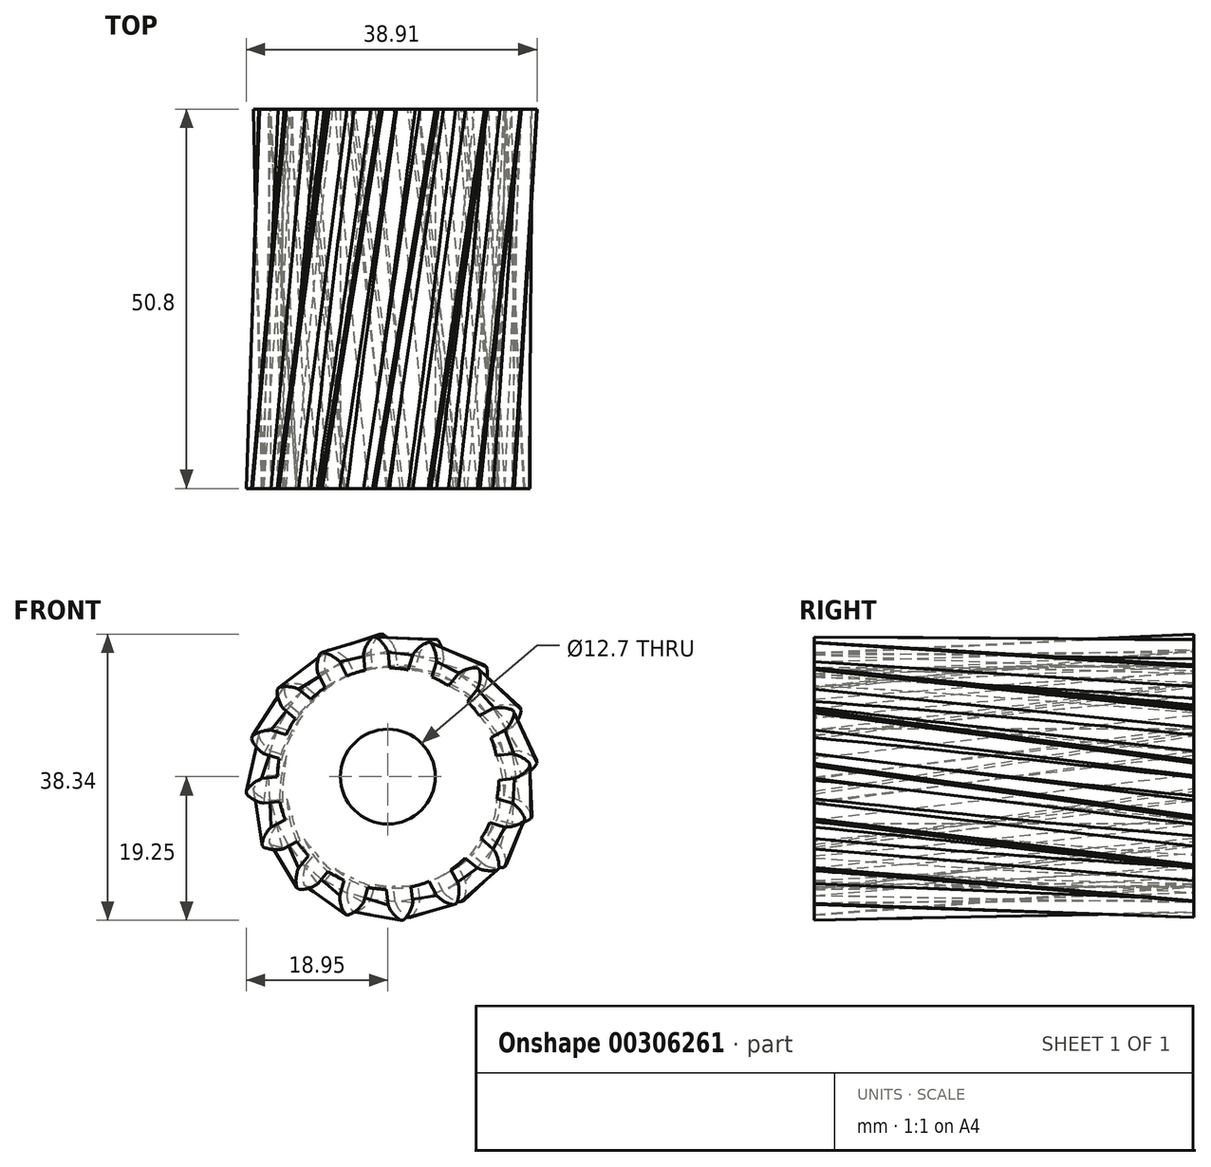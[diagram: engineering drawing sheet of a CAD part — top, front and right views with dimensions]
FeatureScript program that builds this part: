
annotation { "Feature Type Name" : "Feature", "Feature Type Description" : "" }
export const myFeature = defineFeature(function(context is Context, id is Id, definition is map)
    precondition{}
    {
        {
            var Q0;
            Q0=qCreatedBy(makeId("Front.planeOp"),FACE);
            var sketch = newSketch(context, id + "F0", { "sketchPlane" : qUnion([Q0])});
            skCircle(sketch, "E0", {"center": v(0.98, 0.11) * mm, "radius": 14.82 * mm});
            skArc(sketch, "E1.trimOffspring", {"start": v(0.98, 17.04) * mm, "mid": v(0.3, 18.2) * mm, "end": v(-0.7, 19.09) * mm});
            skLineSegment(sketch, "E2", {"start": v(0.98, 17.04) * mm, "end": v(1.19, 14.93) * mm});
            skLineSegment(sketch, "E3", {"start": v(-0.7, 19.09) * mm, "end": v(-0.89, 19.07) * mm});
            skLineSegment(sketch, "E4.MirrorCS", {"start": v(-1.08, 19.05) * mm, "end": v(-0.89, 19.07) * mm});
            skArc(sketch, "E5.MirrorCS", {"start": v(-2.32, 16.71) * mm, "mid": v(-1.89, 17.98) * mm, "end": v(-1.08, 19.05) * mm});
            skLineSegment(sketch, "E6.MirrorCS", {"start": v(-2.32, 16.71) * mm, "end": v(-2.12, 14.6) * mm});
            skPoint(sketch, "E7.orphan", {"position": v(-2, 13.45) * mm});
            skPoint(sketch, "E8.orphan", {"position": v(1.3, 13.77) * mm});
            skLineSegment(sketch, "E9.1.0", {"start": v(-8.43, 14.19) * mm, "end": v(-7.43, 12.32) * mm});
            skArc(sketch, "E9.1.1", {"start": v(-8.43, 14.19) * mm, "mid": v(-8.51, 15.52) * mm, "end": v(-8.17, 16.82) * mm});
            skLineSegment(sketch, "E9.1.2", {"start": v(-7.83, 17) * mm, "end": v(-8, 16.91) * mm});
            skLineSegment(sketch, "E9.1.3", {"start": v(-8.17, 16.82) * mm, "end": v(-8, 16.91) * mm});
            skArc(sketch, "E9.1.4", {"start": v(-5.5, 15.75) * mm, "mid": v(-6.56, 16.56) * mm, "end": v(-7.83, 17) * mm});
            skLineSegment(sketch, "E9.1.5", {"start": v(-5.5, 15.75) * mm, "end": v(-4.5, 13.88) * mm});
            skLineSegment(sketch, "E9.2.0", {"start": v(-13.1, 9.52) * mm, "end": v(-11.46, 8.17) * mm});
            skArc(sketch, "E9.2.1", {"start": v(-13.1, 9.52) * mm, "mid": v(-13.69, 10.72) * mm, "end": v(-13.87, 12.04) * mm});
            skLineSegment(sketch, "E9.2.2", {"start": v(-13.62, 12.35) * mm, "end": v(-13.75, 12.2) * mm});
            skLineSegment(sketch, "E9.2.3", {"start": v(-13.87, 12.04) * mm, "end": v(-13.75, 12.2) * mm});
            skArc(sketch, "E9.2.4", {"start": v(-11, 12.08) * mm, "mid": v(-12.29, 12.42) * mm, "end": v(-13.62, 12.35) * mm});
            skLineSegment(sketch, "E9.2.5", {"start": v(-11, 12.08) * mm, "end": v(-9.35, 10.74) * mm});
            skLineSegment(sketch, "E9.3.0", {"start": v(-15.62, 3.41) * mm, "end": v(-13.6, 2.8) * mm});
            skArc(sketch, "E9.3.1", {"start": v(-15.62, 3.41) * mm, "mid": v(-16.63, 4.3) * mm, "end": v(-17.3, 5.45) * mm});
            skLineSegment(sketch, "E9.3.2", {"start": v(-17.2, 5.83) * mm, "end": v(-17.25, 5.64) * mm});
            skLineSegment(sketch, "E9.3.3", {"start": v(-17.3, 5.45) * mm, "end": v(-17.25, 5.64) * mm});
            skArc(sketch, "E9.3.4", {"start": v(-14.66, 6.59) * mm, "mid": v(-15.99, 6.41) * mm, "end": v(-17.2, 5.83) * mm});
            skLineSegment(sketch, "E9.3.5", {"start": v(-14.66, 6.59) * mm, "end": v(-12.63, 5.97) * mm});
            skLineSegment(sketch, "E9.4.0", {"start": v(-15.62, -3.2) * mm, "end": v(-13.52, -2.98) * mm});
            skArc(sketch, "E9.4.1", {"start": v(-15.62, -3.2) * mm, "mid": v(-16.9, -2.76) * mm, "end": v(-17.96, -1.95) * mm});
            skLineSegment(sketch, "E9.4.2", {"start": v(-18, -1.56) * mm, "end": v(-17.98, -1.76) * mm});
            skLineSegment(sketch, "E9.4.3", {"start": v(-17.96, -1.95) * mm, "end": v(-17.98, -1.76) * mm});
            skArc(sketch, "E9.4.4", {"start": v(-15.95, 0.11) * mm, "mid": v(-17.1, -0.56) * mm, "end": v(-18, -1.56) * mm});
            skLineSegment(sketch, "E9.4.5", {"start": v(-15.95, 0.11) * mm, "end": v(-13.84, 0.32) * mm});
            skLineSegment(sketch, "E9.5.0", {"start": v(-13.1, -9.3) * mm, "end": v(-11.23, -8.3) * mm});
            skArc(sketch, "E9.5.1", {"start": v(-13.1, -9.3) * mm, "mid": v(-14.43, -9.38) * mm, "end": v(-15.73, -9.04) * mm});
            skLineSegment(sketch, "E9.5.2", {"start": v(-15.91, -8.7) * mm, "end": v(-15.82, -8.87) * mm});
            skLineSegment(sketch, "E9.5.3", {"start": v(-15.73, -9.04) * mm, "end": v(-15.82, -8.87) * mm});
            skArc(sketch, "E9.5.4", {"start": v(-14.66, -6.37) * mm, "mid": v(-15.47, -7.43) * mm, "end": v(-15.91, -8.7) * mm});
            skLineSegment(sketch, "E9.5.5", {"start": v(-14.66, -6.37) * mm, "end": v(-12.8, -5.37) * mm});
            skLineSegment(sketch, "E9.6.0", {"start": v(-8.43, -13.97) * mm, "end": v(-7.08, -12.33) * mm});
            skArc(sketch, "E9.6.1", {"start": v(-8.43, -13.97) * mm, "mid": v(-9.63, -14.55) * mm, "end": v(-10.95, -14.74) * mm});
            skLineSegment(sketch, "E9.6.2", {"start": v(-11.26, -14.5) * mm, "end": v(-11.1, -14.62) * mm});
            skLineSegment(sketch, "E9.6.3", {"start": v(-10.95, -14.74) * mm, "end": v(-11.1, -14.62) * mm});
            skArc(sketch, "E9.6.4", {"start": v(-11, -11.86) * mm, "mid": v(-11.33, -13.15) * mm, "end": v(-11.26, -14.5) * mm});
            skLineSegment(sketch, "E9.6.5", {"start": v(-11, -11.86) * mm, "end": v(-9.65, -10.22) * mm});
            skLineSegment(sketch, "E9.7.0", {"start": v(-2.32, -16.5) * mm, "end": v(-1.7, -14.46) * mm});
            skArc(sketch, "E9.7.1", {"start": v(-2.32, -16.5) * mm, "mid": v(-3.2, -17.5) * mm, "end": v(-4.36, -18.17) * mm});
            skLineSegment(sketch, "E9.7.2", {"start": v(-4.74, -18.06) * mm, "end": v(-4.55, -18.12) * mm});
            skLineSegment(sketch, "E9.7.3", {"start": v(-4.36, -18.17) * mm, "end": v(-4.55, -18.12) * mm});
            skArc(sketch, "E9.7.4", {"start": v(-5.5, -15.53) * mm, "mid": v(-5.32, -16.86) * mm, "end": v(-4.74, -18.06) * mm});
            skLineSegment(sketch, "E9.7.5", {"start": v(-5.5, -15.53) * mm, "end": v(-4.88, -13.5) * mm});
            skLineSegment(sketch, "E9.8.0", {"start": v(4.28, -16.5) * mm, "end": v(4.07, -14.38) * mm});
            skArc(sketch, "E9.8.1", {"start": v(4.28, -16.5) * mm, "mid": v(3.85, -17.76) * mm, "end": v(3.04, -18.83) * mm});
            skLineSegment(sketch, "E9.8.2", {"start": v(2.65, -18.87) * mm, "end": v(2.85, -18.85) * mm});
            skLineSegment(sketch, "E9.8.3", {"start": v(3.04, -18.83) * mm, "end": v(2.85, -18.85) * mm});
            skArc(sketch, "E9.8.4", {"start": v(0.98, -16.82) * mm, "mid": v(1.65, -17.98) * mm, "end": v(2.65, -18.87) * mm});
            skLineSegment(sketch, "E9.8.5", {"start": v(0.98, -16.82) * mm, "end": v(0.77, -14.7) * mm});
            skLineSegment(sketch, "E9.9.0", {"start": v(10.38, -13.97) * mm, "end": v(9.39, -12.1) * mm});
            skArc(sketch, "E9.9.1", {"start": v(10.38, -13.97) * mm, "mid": v(10.47, -15.3) * mm, "end": v(10.13, -16.6) * mm});
            skLineSegment(sketch, "E9.9.2", {"start": v(9.79, -16.78) * mm, "end": v(9.96, -16.7) * mm});
            skLineSegment(sketch, "E9.9.3", {"start": v(10.13, -16.6) * mm, "end": v(9.96, -16.7) * mm});
            skArc(sketch, "E9.9.4", {"start": v(7.46, -15.53) * mm, "mid": v(8.52, -16.34) * mm, "end": v(9.79, -16.78) * mm});
            skLineSegment(sketch, "E9.9.5", {"start": v(7.46, -15.53) * mm, "end": v(6.46, -13.66) * mm});
            skLineSegment(sketch, "E9.10.0", {"start": v(15.06, -9.3) * mm, "end": v(13.42, -7.95) * mm});
            skArc(sketch, "E9.10.1", {"start": v(15.06, -9.3) * mm, "mid": v(15.64, -10.5) * mm, "end": v(15.83, -11.82) * mm});
            skLineSegment(sketch, "E9.10.2", {"start": v(15.58, -12.12) * mm, "end": v(15.7, -11.97) * mm});
            skLineSegment(sketch, "E9.10.3", {"start": v(15.83, -11.82) * mm, "end": v(15.7, -11.97) * mm});
            skArc(sketch, "E9.10.4", {"start": v(12.95, -11.86) * mm, "mid": v(14.24, -12.2) * mm, "end": v(15.58, -12.12) * mm});
            skLineSegment(sketch, "E9.10.5", {"start": v(12.95, -11.86) * mm, "end": v(11.31, -10.51) * mm});
            skLineSegment(sketch, "E9.11.0", {"start": v(17.58, -3.2) * mm, "end": v(15.55, -2.58) * mm});
            skArc(sketch, "E9.11.1", {"start": v(17.58, -3.2) * mm, "mid": v(18.59, -4.08) * mm, "end": v(19.26, -5.23) * mm});
            skLineSegment(sketch, "E9.11.2", {"start": v(19.15, -5.6) * mm, "end": v(19.2, -5.42) * mm});
            skLineSegment(sketch, "E9.11.3", {"start": v(19.26, -5.23) * mm, "end": v(19.2, -5.42) * mm});
            skArc(sketch, "E9.11.4", {"start": v(16.62, -6.37) * mm, "mid": v(17.95, -6.19) * mm, "end": v(19.15, -5.6) * mm});
            skLineSegment(sketch, "E9.11.5", {"start": v(16.62, -6.37) * mm, "end": v(14.6, -5.75) * mm});
            skLineSegment(sketch, "E9.12.0", {"start": v(17.58, 3.41) * mm, "end": v(15.47, 3.2) * mm});
            skArc(sketch, "E9.12.1", {"start": v(17.58, 3.41) * mm, "mid": v(18.85, 2.98) * mm, "end": v(19.92, 2.17) * mm});
            skLineSegment(sketch, "E9.12.2", {"start": v(19.96, 1.78) * mm, "end": v(19.94, 1.98) * mm});
            skLineSegment(sketch, "E9.12.3", {"start": v(19.92, 2.17) * mm, "end": v(19.94, 1.98) * mm});
            skArc(sketch, "E9.12.4", {"start": v(17.9, 0.11) * mm, "mid": v(19.07, 0.78) * mm, "end": v(19.96, 1.78) * mm});
            skLineSegment(sketch, "E9.12.5", {"start": v(17.9, 0.11) * mm, "end": v(15.8, -0.1) * mm});
            skLineSegment(sketch, "E9.13.0", {"start": v(15.06, 9.52) * mm, "end": v(13.19, 8.52) * mm});
            skArc(sketch, "E9.13.1", {"start": v(15.06, 9.52) * mm, "mid": v(16.4, 9.6) * mm, "end": v(17.69, 9.26) * mm});
            skLineSegment(sketch, "E9.13.2", {"start": v(17.87, 8.92) * mm, "end": v(17.78, 9.1) * mm});
            skLineSegment(sketch, "E9.13.3", {"start": v(17.69, 9.26) * mm, "end": v(17.78, 9.1) * mm});
            skArc(sketch, "E9.13.4", {"start": v(16.62, 6.59) * mm, "mid": v(17.43, 7.65) * mm, "end": v(17.87, 8.92) * mm});
            skLineSegment(sketch, "E9.13.5", {"start": v(16.62, 6.59) * mm, "end": v(14.75, 5.6) * mm});
            skLineSegment(sketch, "E9.14.0", {"start": v(10.38, 14.19) * mm, "end": v(9.04, 12.55) * mm});
            skArc(sketch, "E9.14.1", {"start": v(10.38, 14.19) * mm, "mid": v(11.59, 14.78) * mm, "end": v(12.91, 14.96) * mm});
            skLineSegment(sketch, "E9.14.2", {"start": v(13.21, 14.71) * mm, "end": v(13.06, 14.84) * mm});
            skLineSegment(sketch, "E9.14.3", {"start": v(12.91, 14.96) * mm, "end": v(13.06, 14.84) * mm});
            skArc(sketch, "E9.14.4", {"start": v(12.95, 12.08) * mm, "mid": v(13.3, 13.38) * mm, "end": v(13.21, 14.71) * mm});
            skLineSegment(sketch, "E9.14.5", {"start": v(12.95, 12.08) * mm, "end": v(11.6, 10.44) * mm});
            skLineSegment(sketch, "E9.15.0", {"start": v(4.28, 16.71) * mm, "end": v(3.67, 14.69) * mm});
            skArc(sketch, "E9.15.1", {"start": v(4.28, 16.71) * mm, "mid": v(5.17, 17.72) * mm, "end": v(6.32, 18.4) * mm});
            skLineSegment(sketch, "E9.15.2", {"start": v(6.7, 18.28) * mm, "end": v(6.5, 18.34) * mm});
            skLineSegment(sketch, "E9.15.3", {"start": v(6.32, 18.4) * mm, "end": v(6.5, 18.34) * mm});
            skArc(sketch, "E9.15.4", {"start": v(7.46, 15.75) * mm, "mid": v(7.28, 17.08) * mm, "end": v(6.7, 18.28) * mm});
            skLineSegment(sketch, "E9.15.5", {"start": v(7.46, 15.75) * mm, "end": v(6.84, 13.72) * mm});
            skSolve(sketch);
        }
        {
            var Q0;
            Q0=qCreatedBy(makeId("Front.planeOp"),FACE);
            cPlane(context, id + "F1", {"entities" : qUnion([Q0]), "cplaneType" : CPlaneType.OFFSET, "offset" : 50.8 * mm, "width" : 152.4 * mm, "height" : 152.4 * mm});
        }
        {
            var Q0;
            Q0=qCreatedBy(id+"F1.planeOp",FACE);
            var sketch = newSketch(context, id + "F2", { "sketchPlane" : qUnion([Q0])});
            skCircle(sketch, "E10", {"center": v(0.03, -0.27) * mm, "radius": 14.82 * mm});
            skArc(sketch, "E11.trimOffspring", {"start": v(0.03, 16.66) * mm, "mid": v(-0.65, 17.82) * mm, "end": v(-1.65, 18.7) * mm});
            skLineSegment(sketch, "E12", {"start": v(0.03, 16.66) * mm, "end": v(0.23, 14.55) * mm});
            skLineSegment(sketch, "E13", {"start": v(-1.65, 18.7) * mm, "end": v(-1.84, 18.69) * mm});
            skLineSegment(sketch, "E14.MirrorCS", {"start": v(-2.03, 18.67) * mm, "end": v(-1.84, 18.69) * mm});
            skArc(sketch, "E15.MirrorCS", {"start": v(-3.28, 16.33) * mm, "mid": v(-2.84, 17.6) * mm, "end": v(-2.03, 18.67) * mm});
            skLineSegment(sketch, "E16.MirrorCS", {"start": v(-3.28, 16.33) * mm, "end": v(-3.07, 14.22) * mm});
            skPoint(sketch, "E17.orphan", {"position": v(-2.95, 13.07) * mm});
            skPoint(sketch, "E18.orphan", {"position": v(0.35, 13.4) * mm});
            skLineSegment(sketch, "E19.1.0", {"start": v(-9.38, 13.8) * mm, "end": v(-8.38, 11.94) * mm});
            skArc(sketch, "E19.1.1", {"start": v(-9.38, 13.8) * mm, "mid": v(-9.46, 15.14) * mm, "end": v(-9.12, 16.44) * mm});
            skLineSegment(sketch, "E19.1.2", {"start": v(-8.78, 16.62) * mm, "end": v(-8.95, 16.53) * mm});
            skLineSegment(sketch, "E19.1.3", {"start": v(-9.12, 16.44) * mm, "end": v(-8.95, 16.53) * mm});
            skArc(sketch, "E19.1.4", {"start": v(-6.45, 15.37) * mm, "mid": v(-7.52, 16.18) * mm, "end": v(-8.78, 16.62) * mm});
            skLineSegment(sketch, "E19.1.5", {"start": v(-6.45, 15.37) * mm, "end": v(-5.45, 13.5) * mm});
            skLineSegment(sketch, "E19.2.0", {"start": v(-14.05, 9.14) * mm, "end": v(-12.41, 7.8) * mm});
            skArc(sketch, "E19.2.1", {"start": v(-14.05, 9.14) * mm, "mid": v(-14.64, 10.34) * mm, "end": v(-14.82, 11.66) * mm});
            skLineSegment(sketch, "E19.2.2", {"start": v(-14.57, 11.97) * mm, "end": v(-14.7, 11.82) * mm});
            skLineSegment(sketch, "E19.2.3", {"start": v(-14.82, 11.66) * mm, "end": v(-14.7, 11.82) * mm});
            skArc(sketch, "E19.2.4", {"start": v(-11.94, 11.7) * mm, "mid": v(-13.24, 12.04) * mm, "end": v(-14.57, 11.97) * mm});
            skLineSegment(sketch, "E19.2.5", {"start": v(-11.94, 11.7) * mm, "end": v(-10.3, 10.36) * mm});
            skLineSegment(sketch, "E19.3.0", {"start": v(-16.58, 3.03) * mm, "end": v(-14.55, 2.42) * mm});
            skArc(sketch, "E19.3.1", {"start": v(-16.58, 3.03) * mm, "mid": v(-17.58, 3.92) * mm, "end": v(-18.26, 5.07) * mm});
            skLineSegment(sketch, "E19.3.2", {"start": v(-18.15, 5.45) * mm, "end": v(-18.2, 5.26) * mm});
            skLineSegment(sketch, "E19.3.3", {"start": v(-18.26, 5.07) * mm, "end": v(-18.2, 5.26) * mm});
            skArc(sketch, "E19.3.4", {"start": v(-15.61, 6.2) * mm, "mid": v(-16.94, 6.03) * mm, "end": v(-18.15, 5.45) * mm});
            skLineSegment(sketch, "E19.3.5", {"start": v(-15.61, 6.2) * mm, "end": v(-13.59, 5.6) * mm});
            skLineSegment(sketch, "E19.4.0", {"start": v(-16.58, -3.57) * mm, "end": v(-14.47, -3.36) * mm});
            skArc(sketch, "E19.4.1", {"start": v(-16.58, -3.57) * mm, "mid": v(-17.84, -3.14) * mm, "end": v(-18.91, -2.33) * mm});
            skLineSegment(sketch, "E19.4.2", {"start": v(-18.95, -1.94) * mm, "end": v(-18.93, -2.14) * mm});
            skLineSegment(sketch, "E19.4.3", {"start": v(-18.91, -2.33) * mm, "end": v(-18.93, -2.14) * mm});
            skArc(sketch, "E19.4.4", {"start": v(-16.9, -0.27) * mm, "mid": v(-18.06, -0.94) * mm, "end": v(-18.95, -1.94) * mm});
            skLineSegment(sketch, "E19.4.5", {"start": v(-16.9, -0.27) * mm, "end": v(-14.8, -0.06) * mm});
            skLineSegment(sketch, "E19.5.0", {"start": v(-14.05, -9.68) * mm, "end": v(-12.18, -8.68) * mm});
            skArc(sketch, "E19.5.1", {"start": v(-14.05, -9.68) * mm, "mid": v(-15.39, -9.76) * mm, "end": v(-16.68, -9.42) * mm});
            skLineSegment(sketch, "E19.5.2", {"start": v(-16.87, -9.08) * mm, "end": v(-16.77, -9.25) * mm});
            skLineSegment(sketch, "E19.5.3", {"start": v(-16.68, -9.42) * mm, "end": v(-16.77, -9.25) * mm});
            skArc(sketch, "E19.5.4", {"start": v(-15.61, -6.75) * mm, "mid": v(-16.43, -7.81) * mm, "end": v(-16.87, -9.08) * mm});
            skLineSegment(sketch, "E19.5.5", {"start": v(-15.61, -6.75) * mm, "end": v(-13.74, -5.75) * mm});
            skLineSegment(sketch, "E19.6.0", {"start": v(-9.38, -14.35) * mm, "end": v(-8.03, -12.7) * mm});
            skArc(sketch, "E19.6.1", {"start": v(-9.38, -14.35) * mm, "mid": v(-10.58, -14.94) * mm, "end": v(-11.9, -15.12) * mm});
            skLineSegment(sketch, "E19.6.2", {"start": v(-12.2, -14.87) * mm, "end": v(-12.06, -15) * mm});
            skLineSegment(sketch, "E19.6.3", {"start": v(-11.9, -15.12) * mm, "end": v(-12.06, -15) * mm});
            skArc(sketch, "E19.6.4", {"start": v(-11.94, -12.24) * mm, "mid": v(-12.29, -13.53) * mm, "end": v(-12.2, -14.87) * mm});
            skLineSegment(sketch, "E19.6.5", {"start": v(-11.94, -12.24) * mm, "end": v(-10.6, -10.6) * mm});
            skLineSegment(sketch, "E19.7.0", {"start": v(-3.28, -16.87) * mm, "end": v(-2.66, -14.85) * mm});
            skArc(sketch, "E19.7.1", {"start": v(-3.28, -16.87) * mm, "mid": v(-4.16, -17.88) * mm, "end": v(-5.32, -18.56) * mm});
            skLineSegment(sketch, "E19.7.2", {"start": v(-5.69, -18.44) * mm, "end": v(-5.5, -18.5) * mm});
            skLineSegment(sketch, "E19.7.3", {"start": v(-5.32, -18.56) * mm, "end": v(-5.5, -18.5) * mm});
            skArc(sketch, "E19.7.4", {"start": v(-6.45, -15.91) * mm, "mid": v(-6.27, -17.24) * mm, "end": v(-5.69, -18.44) * mm});
            skLineSegment(sketch, "E19.7.5", {"start": v(-6.45, -15.91) * mm, "end": v(-5.84, -13.88) * mm});
            skLineSegment(sketch, "E19.8.0", {"start": v(3.33, -16.87) * mm, "end": v(3.12, -14.76) * mm});
            skArc(sketch, "E19.8.1", {"start": v(3.33, -16.87) * mm, "mid": v(2.9, -18.14) * mm, "end": v(2.09, -19.2) * mm});
            skLineSegment(sketch, "E19.8.2", {"start": v(1.7, -19.25) * mm, "end": v(1.9, -19.23) * mm});
            skLineSegment(sketch, "E19.8.3", {"start": v(2.09, -19.2) * mm, "end": v(1.9, -19.23) * mm});
            skArc(sketch, "E19.8.4", {"start": v(0.03, -17.2) * mm, "mid": v(0.7, -18.36) * mm, "end": v(1.7, -19.25) * mm});
            skLineSegment(sketch, "E19.8.5", {"start": v(0.03, -17.2) * mm, "end": v(-0.18, -15.09) * mm});
            skLineSegment(sketch, "E19.9.0", {"start": v(9.43, -14.35) * mm, "end": v(8.43, -12.48) * mm});
            skArc(sketch, "E19.9.1", {"start": v(9.43, -14.35) * mm, "mid": v(9.52, -15.68) * mm, "end": v(9.18, -16.98) * mm});
            skLineSegment(sketch, "E19.9.2", {"start": v(8.83, -17.16) * mm, "end": v(9, -17.07) * mm});
            skLineSegment(sketch, "E19.9.3", {"start": v(9.18, -16.98) * mm, "end": v(9, -17.07) * mm});
            skArc(sketch, "E19.9.4", {"start": v(6.5, -15.91) * mm, "mid": v(7.57, -16.72) * mm, "end": v(8.83, -17.16) * mm});
            skLineSegment(sketch, "E19.9.5", {"start": v(6.5, -15.91) * mm, "end": v(5.5, -14.04) * mm});
            skLineSegment(sketch, "E19.10.0", {"start": v(14.1, -9.68) * mm, "end": v(12.46, -8.33) * mm});
            skArc(sketch, "E19.10.1", {"start": v(14.1, -9.68) * mm, "mid": v(14.7, -10.88) * mm, "end": v(14.88, -12.2) * mm});
            skLineSegment(sketch, "E19.10.2", {"start": v(14.63, -12.5) * mm, "end": v(14.75, -12.36) * mm});
            skLineSegment(sketch, "E19.10.3", {"start": v(14.88, -12.2) * mm, "end": v(14.75, -12.36) * mm});
            skArc(sketch, "E19.10.4", {"start": v(12, -12.24) * mm, "mid": v(13.3, -12.58) * mm, "end": v(14.63, -12.5) * mm});
            skLineSegment(sketch, "E19.10.5", {"start": v(12, -12.24) * mm, "end": v(10.36, -10.9) * mm});
            skLineSegment(sketch, "E19.11.0", {"start": v(16.63, -3.57) * mm, "end": v(14.6, -2.96) * mm});
            skArc(sketch, "E19.11.1", {"start": v(16.63, -3.57) * mm, "mid": v(17.63, -4.46) * mm, "end": v(18.31, -5.61) * mm});
            skLineSegment(sketch, "E19.11.2", {"start": v(18.2, -5.99) * mm, "end": v(18.26, -5.8) * mm});
            skLineSegment(sketch, "E19.11.3", {"start": v(18.31, -5.61) * mm, "end": v(18.26, -5.8) * mm});
            skArc(sketch, "E19.11.4", {"start": v(15.67, -6.75) * mm, "mid": v(17, -6.57) * mm, "end": v(18.2, -5.99) * mm});
            skLineSegment(sketch, "E19.11.5", {"start": v(15.67, -6.75) * mm, "end": v(13.64, -6.13) * mm});
            skLineSegment(sketch, "E19.12.0", {"start": v(16.63, 3.03) * mm, "end": v(14.52, 2.82) * mm});
            skArc(sketch, "E19.12.1", {"start": v(16.63, 3.03) * mm, "mid": v(17.9, 2.6) * mm, "end": v(18.96, 1.8) * mm});
            skLineSegment(sketch, "E19.12.2", {"start": v(19, 1.4) * mm, "end": v(18.99, 1.6) * mm});
            skLineSegment(sketch, "E19.12.3", {"start": v(18.96, 1.8) * mm, "end": v(18.99, 1.6) * mm});
            skArc(sketch, "E19.12.4", {"start": v(16.96, -0.27) * mm, "mid": v(18.11, 0.4) * mm, "end": v(19, 1.4) * mm});
            skLineSegment(sketch, "E19.12.5", {"start": v(16.96, -0.27) * mm, "end": v(14.85, -0.48) * mm});
            skLineSegment(sketch, "E19.13.0", {"start": v(14.1, 9.14) * mm, "end": v(12.23, 8.14) * mm});
            skArc(sketch, "E19.13.1", {"start": v(14.1, 9.14) * mm, "mid": v(15.44, 9.22) * mm, "end": v(16.73, 8.88) * mm});
            skLineSegment(sketch, "E19.13.2", {"start": v(16.92, 8.54) * mm, "end": v(16.83, 8.71) * mm});
            skLineSegment(sketch, "E19.13.3", {"start": v(16.73, 8.88) * mm, "end": v(16.83, 8.71) * mm});
            skArc(sketch, "E19.13.4", {"start": v(15.67, 6.2) * mm, "mid": v(16.48, 7.27) * mm, "end": v(16.92, 8.54) * mm});
            skLineSegment(sketch, "E19.13.5", {"start": v(15.67, 6.2) * mm, "end": v(13.8, 5.2) * mm});
            skLineSegment(sketch, "E19.14.0", {"start": v(9.43, 13.8) * mm, "end": v(8.09, 12.17) * mm});
            skArc(sketch, "E19.14.1", {"start": v(9.43, 13.8) * mm, "mid": v(10.63, 14.4) * mm, "end": v(11.96, 14.58) * mm});
            skLineSegment(sketch, "E19.14.2", {"start": v(12.26, 14.33) * mm, "end": v(12.11, 14.46) * mm});
            skLineSegment(sketch, "E19.14.3", {"start": v(11.96, 14.58) * mm, "end": v(12.11, 14.46) * mm});
            skArc(sketch, "E19.14.4", {"start": v(12, 11.7) * mm, "mid": v(12.34, 13) * mm, "end": v(12.26, 14.33) * mm});
            skLineSegment(sketch, "E19.14.5", {"start": v(12, 11.7) * mm, "end": v(10.65, 10.06) * mm});
            skLineSegment(sketch, "E19.15.0", {"start": v(3.33, 16.33) * mm, "end": v(2.71, 14.3) * mm});
            skArc(sketch, "E19.15.1", {"start": v(3.33, 16.33) * mm, "mid": v(4.21, 17.34) * mm, "end": v(5.37, 18.02) * mm});
            skLineSegment(sketch, "E19.15.2", {"start": v(5.74, 17.9) * mm, "end": v(5.56, 17.96) * mm});
            skLineSegment(sketch, "E19.15.3", {"start": v(5.37, 18.02) * mm, "end": v(5.56, 17.96) * mm});
            skArc(sketch, "E19.15.4", {"start": v(6.5, 15.37) * mm, "mid": v(6.33, 16.7) * mm, "end": v(5.74, 17.9) * mm});
            skLineSegment(sketch, "E19.15.5", {"start": v(6.5, 15.37) * mm, "end": v(5.89, 13.34) * mm});
            skSolve(sketch);
        }
        {
            var Q0;
            Q0=makeQuery(id+"F2.imprint","IMPRINT",FACE,{"disambiguationData":[TD([[makeQuery(id+"F2.imprint","IMPRINT",EDGE,{"derivedFrom":sQuery(id+"F2.wireOp",EDGE,"E11.trimOffspring")}),1.0]])]});
            var Q1;
            {var subQ0=sQuery(id+"F0.wireOp",EDGE,"E9.15.0");Q1=makeQuery(id+"F0.imprint","IMPRINT",FACE,{"disambiguationData":[TD([[makeQuery(id+"F0.imprint","IMPRINT",EDGE,{"derivedFrom":subQ0}),1.0]])]});}
            loft(context, id + "F3", {"sheetProfilesArray" : [{ "sheetProfileEntities" : qUnion([Q0]) }, { "sheetProfileEntities" : qUnion([Q1]) }]});
        }
        {
            var Q1;
            {var subQ0=sQuery(id+"F2.wireOp",EDGE,"E10");var subQ18=makeQuery(id+"F2.imprint","INTERSECT",VERTEX,{"derivedFrom":[subQ0,sQuery(id+"F2.wireOp",EDGE,"E19.12.0")]});Q1=makeQuery(id+"F2.imprint","IMPRINT",FACE,{"disambiguationData":[TD([[makeQuery(id+"F2.imprint","IMPRINT",EDGE,{"disambiguationData":[TD([[subQ18,-1.0]])],"derivedFrom":subQ0}),1.0]])]});}
            var Q2;
            {var subQ0=sQuery(id+"F0.wireOp",EDGE,"E0");var subQ18=makeQuery(id+"F0.imprint","INTERSECT",VERTEX,{"derivedFrom":[subQ0,sQuery(id+"F0.wireOp",EDGE,"E9.12.0")]});Q2=makeQuery(id+"F0.imprint","IMPRINT",FACE,{"disambiguationData":[TD([[makeQuery(id+"F0.imprint","IMPRINT",EDGE,{"disambiguationData":[TD([[subQ18,-1.0]])],"derivedFrom":subQ0}),1.0]])]});}
            loft(context, id + "F4", {"operationType" : NewBodyOperationType.ADD, "sheetProfilesArray" : [{ "sheetProfileEntities" : qUnion([Q1]) }, { "sheetProfileEntities" : qUnion([Q2]) }]});
        }
        {
            var Q1;
            {var subQ0=sQuery(id+"F2.wireOp",EDGE,"E19.15.0");Q1=makeQuery(id+"F2.imprint","IMPRINT",FACE,{"disambiguationData":[TD([[makeQuery(id+"F2.imprint","IMPRINT",EDGE,{"derivedFrom":subQ0}),1.0]])]});}
            var Q2;
            {var subQ0=sQuery(id+"F0.wireOp",EDGE,"E9.14.0");Q2=makeQuery(id+"F0.imprint","IMPRINT",FACE,{"disambiguationData":[TD([[makeQuery(id+"F0.imprint","IMPRINT",EDGE,{"derivedFrom":subQ0}),1.0]])]});}
            loft(context, id + "F5", {"operationType" : NewBodyOperationType.ADD, "sheetProfilesArray" : [{ "sheetProfileEntities" : qUnion([Q1]) }, { "sheetProfileEntities" : qUnion([Q2]) }]});
        }
        {
            var Q1;
            {var subQ0=sQuery(id+"F2.wireOp",EDGE,"E19.14.0");Q1=makeQuery(id+"F2.imprint","IMPRINT",FACE,{"disambiguationData":[TD([[makeQuery(id+"F2.imprint","IMPRINT",EDGE,{"derivedFrom":subQ0}),1.0]])]});}
            var Q2;
            {var subQ0=sQuery(id+"F0.wireOp",EDGE,"E9.13.0");Q2=makeQuery(id+"F0.imprint","IMPRINT",FACE,{"disambiguationData":[TD([[makeQuery(id+"F0.imprint","IMPRINT",EDGE,{"derivedFrom":subQ0}),1.0]])]});}
            loft(context, id + "F6", {"operationType" : NewBodyOperationType.ADD, "sheetProfilesArray" : [{ "sheetProfileEntities" : qUnion([Q1]) }, { "sheetProfileEntities" : qUnion([Q2]) }]});
        }
        {
            var Q1;
            {var subQ0=sQuery(id+"F2.wireOp",EDGE,"E19.13.0");Q1=makeQuery(id+"F2.imprint","IMPRINT",FACE,{"disambiguationData":[TD([[makeQuery(id+"F2.imprint","IMPRINT",EDGE,{"derivedFrom":subQ0}),1.0]])]});}
            var Q2;
            {var subQ0=sQuery(id+"F0.wireOp",EDGE,"E9.12.0");Q2=makeQuery(id+"F0.imprint","IMPRINT",FACE,{"disambiguationData":[TD([[makeQuery(id+"F0.imprint","IMPRINT",EDGE,{"derivedFrom":subQ0}),1.0]])]});}
            loft(context, id + "F7", {"operationType" : NewBodyOperationType.ADD, "sheetProfilesArray" : [{ "sheetProfileEntities" : qUnion([Q1]) }, { "sheetProfileEntities" : qUnion([Q2]) }]});
        }
        {
            var Q1;
            {var subQ0=sQuery(id+"F2.wireOp",EDGE,"E19.12.0");Q1=makeQuery(id+"F2.imprint","IMPRINT",FACE,{"disambiguationData":[TD([[makeQuery(id+"F2.imprint","IMPRINT",EDGE,{"derivedFrom":subQ0}),1.0]])]});}
            var Q2;
            {var subQ0=sQuery(id+"F0.wireOp",EDGE,"E9.11.0");Q2=makeQuery(id+"F0.imprint","IMPRINT",FACE,{"disambiguationData":[TD([[makeQuery(id+"F0.imprint","IMPRINT",EDGE,{"derivedFrom":subQ0}),1.0]])]});}
            loft(context, id + "F8", {"operationType" : NewBodyOperationType.ADD, "sheetProfilesArray" : [{ "sheetProfileEntities" : qUnion([Q1]) }, { "sheetProfileEntities" : qUnion([Q2]) }]});
        }
        {
            var Q1;
            {var subQ0=sQuery(id+"F2.wireOp",EDGE,"E19.11.0");Q1=makeQuery(id+"F2.imprint","IMPRINT",FACE,{"disambiguationData":[TD([[makeQuery(id+"F2.imprint","IMPRINT",EDGE,{"derivedFrom":subQ0}),1.0]])]});}
            var Q2;
            {var subQ0=sQuery(id+"F0.wireOp",EDGE,"E9.10.0");Q2=makeQuery(id+"F0.imprint","IMPRINT",FACE,{"disambiguationData":[TD([[makeQuery(id+"F0.imprint","IMPRINT",EDGE,{"derivedFrom":subQ0}),1.0]])]});}
            loft(context, id + "F9", {"operationType" : NewBodyOperationType.ADD, "sheetProfilesArray" : [{ "sheetProfileEntities" : qUnion([Q1]) }, { "sheetProfileEntities" : qUnion([Q2]) }]});
        }
        {
            var Q1;
            {var subQ0=sQuery(id+"F2.wireOp",EDGE,"E19.10.0");Q1=makeQuery(id+"F2.imprint","IMPRINT",FACE,{"disambiguationData":[TD([[makeQuery(id+"F2.imprint","IMPRINT",EDGE,{"derivedFrom":subQ0}),1.0]])]});}
            var Q2;
            {var subQ0=sQuery(id+"F0.wireOp",EDGE,"E9.9.0");Q2=makeQuery(id+"F0.imprint","IMPRINT",FACE,{"disambiguationData":[TD([[makeQuery(id+"F0.imprint","IMPRINT",EDGE,{"derivedFrom":subQ0}),1.0]])]});}
            loft(context, id + "F10", {"operationType" : NewBodyOperationType.ADD, "sheetProfilesArray" : [{ "sheetProfileEntities" : qUnion([Q1]) }, { "sheetProfileEntities" : qUnion([Q2]) }]});
        }
        {
            var Q1;
            {var subQ0=sQuery(id+"F2.wireOp",EDGE,"E19.9.0");Q1=makeQuery(id+"F2.imprint","IMPRINT",FACE,{"disambiguationData":[TD([[makeQuery(id+"F2.imprint","IMPRINT",EDGE,{"derivedFrom":subQ0}),1.0]])]});}
            var Q2;
            {var subQ0=sQuery(id+"F0.wireOp",EDGE,"E9.8.0");Q2=makeQuery(id+"F0.imprint","IMPRINT",FACE,{"disambiguationData":[TD([[makeQuery(id+"F0.imprint","IMPRINT",EDGE,{"derivedFrom":subQ0}),1.0]])]});}
            loft(context, id + "F11", {"operationType" : NewBodyOperationType.ADD, "sheetProfilesArray" : [{ "sheetProfileEntities" : qUnion([Q1]) }, { "sheetProfileEntities" : qUnion([Q2]) }]});
        }
        {
            var Q1;
            {var subQ0=sQuery(id+"F2.wireOp",EDGE,"E19.8.0");Q1=makeQuery(id+"F2.imprint","IMPRINT",FACE,{"disambiguationData":[TD([[makeQuery(id+"F2.imprint","IMPRINT",EDGE,{"derivedFrom":subQ0}),1.0]])]});}
            var Q2;
            {var subQ0=sQuery(id+"F0.wireOp",EDGE,"E9.7.0");Q2=makeQuery(id+"F0.imprint","IMPRINT",FACE,{"disambiguationData":[TD([[makeQuery(id+"F0.imprint","IMPRINT",EDGE,{"derivedFrom":subQ0}),1.0]])]});}
            loft(context, id + "F12", {"operationType" : NewBodyOperationType.ADD, "sheetProfilesArray" : [{ "sheetProfileEntities" : qUnion([Q1]) }, { "sheetProfileEntities" : qUnion([Q2]) }]});
        }
        {
            var Q1;
            {var subQ0=sQuery(id+"F2.wireOp",EDGE,"E19.7.0");Q1=makeQuery(id+"F2.imprint","IMPRINT",FACE,{"disambiguationData":[TD([[makeQuery(id+"F2.imprint","IMPRINT",EDGE,{"derivedFrom":subQ0}),1.0]])]});}
            var Q2;
            {var subQ0=sQuery(id+"F0.wireOp",EDGE,"E9.6.0");Q2=makeQuery(id+"F0.imprint","IMPRINT",FACE,{"disambiguationData":[TD([[makeQuery(id+"F0.imprint","IMPRINT",EDGE,{"derivedFrom":subQ0}),1.0]])]});}
            loft(context, id + "F13", {"operationType" : NewBodyOperationType.ADD, "sheetProfilesArray" : [{ "sheetProfileEntities" : qUnion([Q1]) }, { "sheetProfileEntities" : qUnion([Q2]) }]});
        }
        {
            var Q1;
            {var subQ0=sQuery(id+"F2.wireOp",EDGE,"E19.6.0");Q1=makeQuery(id+"F2.imprint","IMPRINT",FACE,{"disambiguationData":[TD([[makeQuery(id+"F2.imprint","IMPRINT",EDGE,{"derivedFrom":subQ0}),1.0]])]});}
            var Q2;
            {var subQ0=sQuery(id+"F0.wireOp",EDGE,"E9.5.0");Q2=makeQuery(id+"F0.imprint","IMPRINT",FACE,{"disambiguationData":[TD([[makeQuery(id+"F0.imprint","IMPRINT",EDGE,{"derivedFrom":subQ0}),1.0]])]});}
            loft(context, id + "F14", {"operationType" : NewBodyOperationType.ADD, "sheetProfilesArray" : [{ "sheetProfileEntities" : qUnion([Q1]) }, { "sheetProfileEntities" : qUnion([Q2]) }]});
        }
        {
            var Q1;
            {var subQ0=sQuery(id+"F2.wireOp",EDGE,"E19.5.0");Q1=makeQuery(id+"F2.imprint","IMPRINT",FACE,{"disambiguationData":[TD([[makeQuery(id+"F2.imprint","IMPRINT",EDGE,{"derivedFrom":subQ0}),1.0]])]});}
            var Q2;
            {var subQ0=sQuery(id+"F0.wireOp",EDGE,"E9.4.0");Q2=makeQuery(id+"F0.imprint","IMPRINT",FACE,{"disambiguationData":[TD([[makeQuery(id+"F0.imprint","IMPRINT",EDGE,{"derivedFrom":subQ0}),1.0]])]});}
            loft(context, id + "F15", {"operationType" : NewBodyOperationType.ADD, "sheetProfilesArray" : [{ "sheetProfileEntities" : qUnion([Q1]) }, { "sheetProfileEntities" : qUnion([Q2]) }]});
        }
        {
            var Q1;
            {var subQ0=sQuery(id+"F2.wireOp",EDGE,"E19.4.0");Q1=makeQuery(id+"F2.imprint","IMPRINT",FACE,{"disambiguationData":[TD([[makeQuery(id+"F2.imprint","IMPRINT",EDGE,{"derivedFrom":subQ0}),1.0]])]});}
            var Q2;
            {var subQ0=sQuery(id+"F0.wireOp",EDGE,"E9.3.0");Q2=makeQuery(id+"F0.imprint","IMPRINT",FACE,{"disambiguationData":[TD([[makeQuery(id+"F0.imprint","IMPRINT",EDGE,{"derivedFrom":subQ0}),1.0]])]});}
            loft(context, id + "F16", {"operationType" : NewBodyOperationType.ADD, "sheetProfilesArray" : [{ "sheetProfileEntities" : qUnion([Q1]) }, { "sheetProfileEntities" : qUnion([Q2]) }]});
        }
        {
            var Q1;
            {var subQ0=sQuery(id+"F2.wireOp",EDGE,"E19.3.0");Q1=makeQuery(id+"F2.imprint","IMPRINT",FACE,{"disambiguationData":[TD([[makeQuery(id+"F2.imprint","IMPRINT",EDGE,{"derivedFrom":subQ0}),1.0]])]});}
            var Q2;
            {var subQ0=sQuery(id+"F0.wireOp",EDGE,"E9.2.0");Q2=makeQuery(id+"F0.imprint","IMPRINT",FACE,{"disambiguationData":[TD([[makeQuery(id+"F0.imprint","IMPRINT",EDGE,{"derivedFrom":subQ0}),1.0]])]});}
            loft(context, id + "F17", {"operationType" : NewBodyOperationType.ADD, "sheetProfilesArray" : [{ "sheetProfileEntities" : qUnion([Q1]) }, { "sheetProfileEntities" : qUnion([Q2]) }]});
        }
        {
            var Q1;
            {var subQ0=sQuery(id+"F2.wireOp",EDGE,"E19.2.0");Q1=makeQuery(id+"F2.imprint","IMPRINT",FACE,{"disambiguationData":[TD([[makeQuery(id+"F2.imprint","IMPRINT",EDGE,{"derivedFrom":subQ0}),1.0]])]});}
            var Q2;
            {var subQ0=sQuery(id+"F0.wireOp",EDGE,"E9.1.0");Q2=makeQuery(id+"F0.imprint","IMPRINT",FACE,{"disambiguationData":[TD([[makeQuery(id+"F0.imprint","IMPRINT",EDGE,{"derivedFrom":subQ0}),1.0]])]});}
            loft(context, id + "F18", {"operationType" : NewBodyOperationType.ADD, "sheetProfilesArray" : [{ "sheetProfileEntities" : qUnion([Q1]) }, { "sheetProfileEntities" : qUnion([Q2]) }]});
        }
        {
            var Q1;
            {var subQ0=sQuery(id+"F2.wireOp",EDGE,"E19.1.0");Q1=makeQuery(id+"F2.imprint","IMPRINT",FACE,{"disambiguationData":[TD([[makeQuery(id+"F2.imprint","IMPRINT",EDGE,{"derivedFrom":subQ0}),1.0]])]});}
            var Q2;
            Q2=makeQuery(id+"F0.imprint","IMPRINT",FACE,{"disambiguationData":[TD([[makeQuery(id+"F0.imprint","IMPRINT",EDGE,{"derivedFrom":sQuery(id+"F0.wireOp",EDGE,"E1.trimOffspring")}),1.0]])]});
            loft(context, id + "F19", {"operationType" : NewBodyOperationType.ADD, "sheetProfilesArray" : [{ "sheetProfileEntities" : qUnion([Q1]) }, { "sheetProfileEntities" : qUnion([Q2]) }]});
        }
        {
            var Q0;
            {var subQ0=sQuery(id+"F2.wireOp",EDGE,"E10");var subQ18=makeQuery(id+"F2.imprint","INTERSECT",VERTEX,{"derivedFrom":[subQ0,sQuery(id+"F2.wireOp",EDGE,"E19.12.0")]});Q0=makeQuery(id+"F2.imprint","IMPRINT",FACE,{"disambiguationData":[TD([[makeQuery(id+"F2.imprint","IMPRINT",EDGE,{"disambiguationData":[TD([[subQ18,-1.0]])],"derivedFrom":subQ0}),1.0]])]});}
            var sketch = newSketch(context, id + "F20", { "sketchPlane" : qUnion([Q0])});
            skCircle(sketch, "E20", {"center": v(0, 0) * mm, "radius": 6.35 * mm});
            skSolve(sketch);
        }
        {
            var Q0;
            Q0 = qSketchRegion(id + "F20", true);
            extrude(context, id + "F21", {"entities" : qUnion([Q0]), "operationType" : NewBodyOperationType.REMOVE, "oppositeDirection" : true, "depth" : 50.8 * mm});
        }
    });
